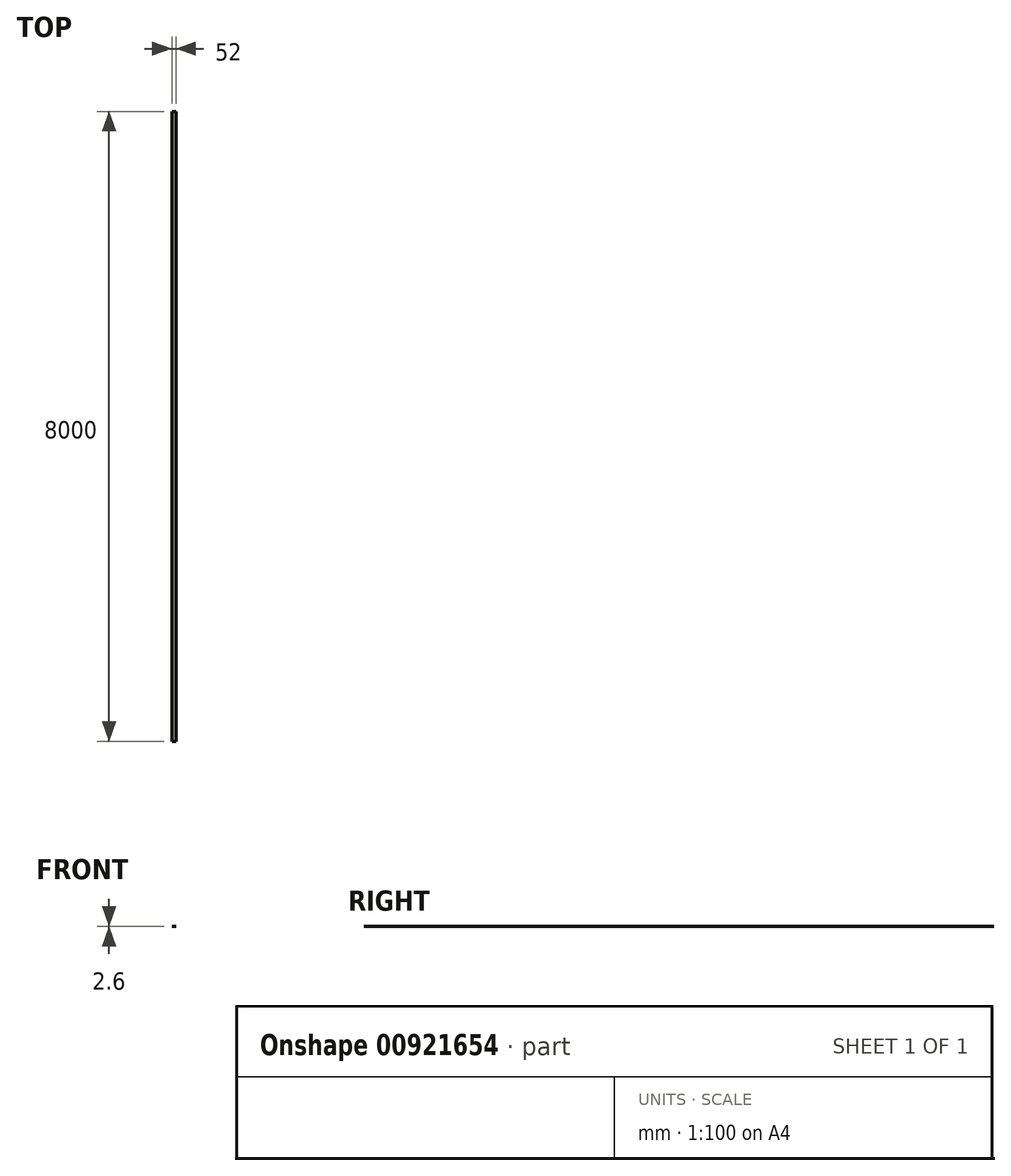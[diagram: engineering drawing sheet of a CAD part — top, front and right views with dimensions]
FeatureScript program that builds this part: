
annotation { "Feature Type Name" : "Feature", "Feature Type Description" : "" }
export const myFeature = defineFeature(function(context is Context, id is Id, definition is map)
    precondition{}
    {
        {
            var Q0;
            Q0=qCreatedBy(makeId("Front.planeOp"),FACE);
            var sketch = newSketch(context, id + "F0", { "sketchPlane" : qUnion([Q0])});
            skLineSegment(sketch, "E0", {"start": v(0, 0) * mm, "end": v(52, 0) * mm});
            skLineSegment(sketch, "E1", {"start": v(52, 0) * mm, "end": v(52, 2.6) * mm});
            skLineSegment(sketch, "E2", {"start": v(52, 2.6) * mm, "end": v(0, 0) * mm});
            skSolve(sketch);
        }
        {
            var Q0;
            Q0 = qSketchRegion(id + "F0", true);
            extrude(context, id + "F1", {"entities" : qUnion([Q0]), "depth" : 8000 * mm, "offsetDistance" : 25 * mm});
        }
    });
